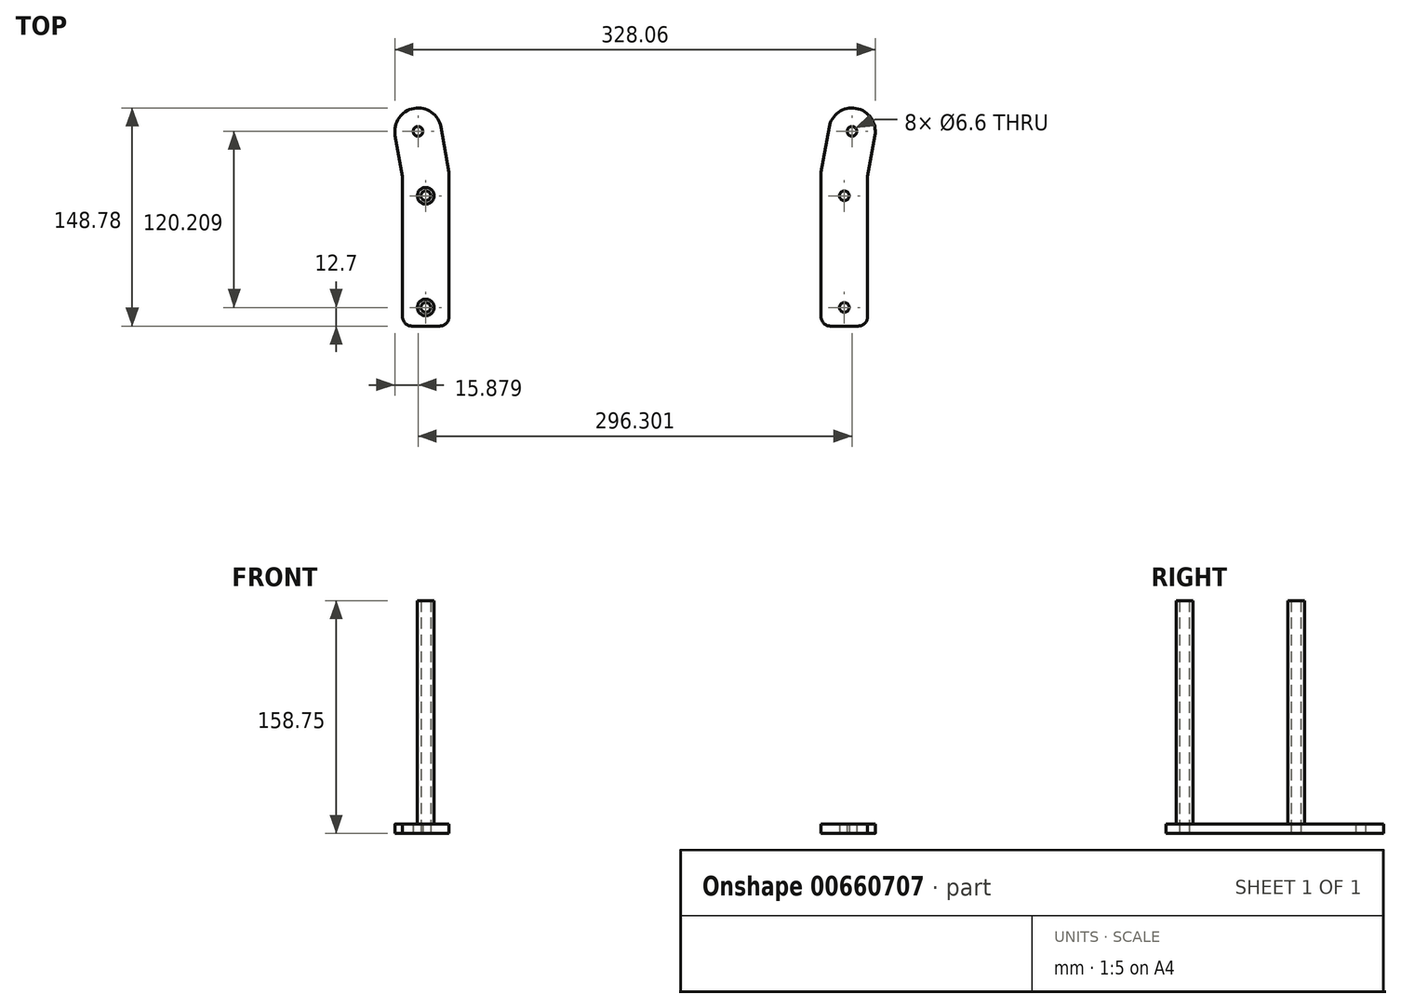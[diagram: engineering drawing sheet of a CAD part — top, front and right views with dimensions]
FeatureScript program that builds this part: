
annotation { "Feature Type Name" : "Feature", "Feature Type Description" : "" }
export const myFeature = defineFeature(function(context is Context, id is Id, definition is map)
    precondition{}
    {
        {
            var Q0;
            Q0=qCreatedBy(makeId("Top.planeOp"),FACE);
            var sketch = newSketch(context, id + "F0", { "sketchPlane" : qUnion([Q0])});
            skLineSegment(sketch, "E0", {"start": v(-163.78, 28.55) * mm, "end": v(-158.85, 0.55) * mm});
            skLineSegment(sketch, "E1", {"start": v(-158.75, -0.56) * mm, "end": v(-158.75, -95.25) * mm});
            skLineSegment(sketch, "E2", {"start": v(-152.4, -101.6) * mm, "end": v(-133.35, -101.6) * mm});
            skLineSegment(sketch, "E3", {"start": v(-127, -95.25) * mm, "end": v(-127, 0) * mm});
            skLineSegment(sketch, "E4", {"start": v(-158.75, 0) * mm, "end": v(-127, 0) * mm, "construction": true});
            skLineSegment(sketch, "E5", {"start": v(-142.88, 0) * mm, "end": v(-142.88, -101.6) * mm, "construction": true});
            skCircle(sketch, "E6", {"center": v(-142.88, -12.7) * mm, "radius": 3.3 * mm});
            skCircle(sketch, "E7", {"center": v(-142.88, -88.9) * mm, "radius": 3.3 * mm});
            skLineSegment(sketch, "E8", {"start": v(-142.88, -12.7) * mm, "end": v(-142.88, -88.9) * mm, "construction": true});
            skPoint(sketch, "E9", {"position": v(-142.88, -50.8) * mm});
            skLineSegment(sketch, "E10", {"start": v(0, 30.92) * mm, "end": v(0, -30.92) * mm, "construction": true});
            skPoint(sketch, "E11", {"position": v(0, 0) * mm});
            skPoint(sketch, "E12.visualSharp", {"position": v(-127, -101.6) * mm});
            skPoint(sketch, "E13.visualSharp", {"position": v(-158.75, -101.6) * mm});
            skArc(sketch, "E14", {"start": v(-132.52, 34.07) * mm, "mid": v(-150.9, 46.94) * mm, "end": v(-163.78, 28.55) * mm});
            skLineSegment(sketch, "E15", {"start": v(-132.52, 34.07) * mm, "end": v(-163.78, 28.55) * mm, "construction": true});
            skLineSegment(sketch, "E16", {"start": v(-132.52, 34.07) * mm, "end": v(-127.1, 3.32) * mm});
            skLineSegment(sketch, "E17", {"start": v(-127, 0) * mm, "end": v(-127, 2.22) * mm});
            skPoint(sketch, "E18.visualSharp", {"position": v(-127, 2.78) * mm});
            skArc(sketch, "E18.filletArc", {"start": v(-127, 2.22) * mm, "mid": v(-127.02, 2.78) * mm, "end": v(-127.1, 3.32) * mm});
            skPoint(sketch, "E19.visualSharp", {"position": v(-158.75, 0) * mm});
            skArc(sketch, "E19.filletArc", {"start": v(-158.75, -0.56) * mm, "mid": v(-158.77, 0) * mm, "end": v(-158.85, 0.55) * mm});
            skLineSegment(sketch, "E20", {"start": v(0, 0) * mm, "end": v(-127, 0) * mm, "construction": true});
            skLineSegment(sketch, "E21", {"start": v(-142.88, 0) * mm, "end": v(-148.15, 31.3) * mm, "construction": true});
            skArc(sketch, "E22.filletArc", {"start": v(-158.75, -95.25) * mm, "mid": v(-156.9, -99.74) * mm, "end": v(-152.4, -101.6) * mm});
            skArc(sketch, "E23.filletArc", {"start": v(-133.35, -101.6) * mm, "mid": v(-128.86, -99.74) * mm, "end": v(-127, -95.25) * mm});
            skLineSegment(sketch, "E24.MirrorCS", {"start": v(132.52, 34.07) * mm, "end": v(127.1, 3.32) * mm});
            skArc(sketch, "E25.MirrorCS", {"start": v(132.52, 34.07) * mm, "mid": v(150.9, 46.94) * mm, "end": v(163.78, 28.55) * mm});
            skLineSegment(sketch, "E26.MirrorCS", {"start": v(163.78, 28.55) * mm, "end": v(158.85, 0.55) * mm});
            skArc(sketch, "E27.MirrorCS", {"start": v(158.75, -0.56) * mm, "mid": v(158.77, 0) * mm, "end": v(158.85, 0.55) * mm});
            skLineSegment(sketch, "E28.MirrorCS", {"start": v(158.75, -0.56) * mm, "end": v(158.75, -95.25) * mm});
            skArc(sketch, "E29.MirrorCS", {"start": v(127, 2.22) * mm, "mid": v(127.02, 2.78) * mm, "end": v(127.1, 3.32) * mm});
            skLineSegment(sketch, "E30.MirrorCS", {"start": v(127, 0) * mm, "end": v(127, 2.22) * mm});
            skArc(sketch, "E31.MirrorCS", {"start": v(158.75, -95.25) * mm, "mid": v(156.9, -99.74) * mm, "end": v(152.4, -101.6) * mm});
            skLineSegment(sketch, "E32.MirrorCS", {"start": v(152.4, -101.6) * mm, "end": v(133.35, -101.6) * mm});
            skArc(sketch, "E33.MirrorCS", {"start": v(133.35, -101.6) * mm, "mid": v(128.86, -99.74) * mm, "end": v(127, -95.25) * mm});
            skLineSegment(sketch, "E34.MirrorCS", {"start": v(127, -95.25) * mm, "end": v(127, 0) * mm});
            skCircle(sketch, "E35", {"center": v(-148.15, 31.3) * mm, "radius": 3.3 * mm});
            skCircle(sketch, "E36.MirrorC", {"center": v(148.15, 31.3) * mm, "radius": 3.3 * mm});
            skCircle(sketch, "E37.MirrorC", {"center": v(142.88, -12.7) * mm, "radius": 3.3 * mm});
            skCircle(sketch, "E38.MirrorC", {"center": v(142.88, -88.9) * mm, "radius": 3.3 * mm});
            skSolve(sketch);
        }
        {
            var Q0;
            Q0=makeQuery(id+"F0.imprint","IMPRINT",FACE,{"disambiguationData":[TD([[makeQuery(id+"F0.imprint","IMPRINT",EDGE,{"derivedFrom":sQuery(id+"F0.wireOp",EDGE,"E0")}),1.0]])]});
            var Q1;
            Q1=makeQuery(id+"F0.imprint","IMPRINT",FACE,{"disambiguationData":[TD([[makeQuery(id+"F0.imprint","IMPRINT",EDGE,{"derivedFrom":sQuery(id+"F0.wireOp",EDGE,"0249e478-3a88-4d2c-a210-11c1fa801e9a0.MirrorCS")}),-1.0]])]});
            var Q2;
            Q2=makeQuery(id+"F0.imprint","IMPRINT",FACE,{"disambiguationData":[TD([[makeQuery(id+"F0.imprint","IMPRINT",EDGE,{"derivedFrom":sQuery(id+"F0.wireOp",EDGE,"417904c8-6a04-4207-bfcf-ffdcabad85960.MirrorCS")}),-1.0]])]});
            var Q3;
            Q3=makeQuery(id+"F0.imprint","IMPRINT",FACE,{"disambiguationData":[TD([[makeQuery(id+"F0.imprint","IMPRINT",EDGE,{"derivedFrom":sQuery(id+"F0.wireOp",EDGE,"E24.MirrorCS")}),1.0]])]});
            extrude(context, id + "F1", {"entities" : qUnion([Q0, Q1, Q2, Q3]), "depth" : 6.35 * mm, "offsetDistance" : 25.4 * mm});
        }
        {
            var Q0;
            Q0=makeQuery(id+"F1.opExtrude","CAP_FACE",FACE,{"disambiguationData":[OSD([sQuery(id+"F0.wireOp",EDGE,"E0"),sQuery(id+"F0.wireOp",EDGE,"E1"),sQuery(id+"F0.wireOp",EDGE,"E2"),sQuery(id+"F0.wireOp",EDGE,"E3"),sQuery(id+"F0.wireOp",EDGE,"uViVmrJY-JCsh-tP8L-dt5C-8XgPy4Xd0ImP"),sQuery(id+"F0.wireOp",EDGE,"lWO3sbvZ-g1mz-J9B7-t8hw-3GOGxWjmcKuG"),sQuery(id+"F0.wireOp",EDGE,"E6"),sQuery(id+"F0.wireOp",EDGE,"E7")])],"isStart":false});
            var sketch = newSketch(context, id + "F2", { "sketchPlane" : qUnion([Q0])});
            skCircle(sketch, "E39.0", {"center": v(-142.88, -12.7) * mm, "radius": 3.3 * mm});
            skCircle(sketch, "E40.0", {"center": v(-142.88, -88.9) * mm, "radius": 3.3 * mm});
            skCircle(sketch, "E41", {"center": v(-142.88, -12.7) * mm, "radius": 5.72 * mm});
            skCircle(sketch, "E42", {"center": v(-142.88, -88.9) * mm, "radius": 5.72 * mm});
            skLineSegment(sketch, "E43.0", {"start": v(0, 30.92) * mm, "end": v(0, -30.92) * mm});
            skCircle(sketch, "E44.MirrorC", {"center": v(142.88, -12.7) * mm, "radius": 5.72 * mm});
            skCircle(sketch, "E45.MirrorC", {"center": v(142.88, -88.9) * mm, "radius": 5.72 * mm});
            skCircle(sketch, "E46.MirrorC", {"center": v(142.88, -12.7) * mm, "radius": 3.3 * mm});
            skCircle(sketch, "E47.MirrorC", {"center": v(142.88, -88.9) * mm, "radius": 3.3 * mm});
            skSolve(sketch);
        }
        {
            var Q0;
            Q0=makeQuery(id+"F2.imprint","IMPRINT",FACE,{"disambiguationData":[TD([[makeQuery(id+"F2.imprint","IMPRINT",EDGE,{"derivedFrom":sQuery(id+"F2.wireOp",EDGE,"E39.0")}),-1.0]])]});
            var Q1;
            Q1=makeQuery(id+"F2.imprint","IMPRINT",FACE,{"disambiguationData":[TD([[makeQuery(id+"F2.imprint","IMPRINT",EDGE,{"derivedFrom":sQuery(id+"F2.wireOp",EDGE,"E40.0")}),-1.0]])]});
            var Q2;
            Q2=makeQuery(id+"F2.imprint","IMPRINT",FACE,{"disambiguationData":[TD([[makeQuery(id+"F2.imprint","IMPRINT",EDGE,{"derivedFrom":sQuery(id+"F2.wireOp",EDGE,"E44.MirrorC")}),-1.0]])]});
            var Q3;
            Q3=makeQuery(id+"F2.imprint","IMPRINT",FACE,{"disambiguationData":[TD([[makeQuery(id+"F2.imprint","IMPRINT",EDGE,{"derivedFrom":sQuery(id+"F2.wireOp",EDGE,"E45.MirrorC")}),-1.0]])]});
            extrude(context, id + "F3", {"entities" : qUnion([Q0, Q1, Q2, Q3]), "depth" : 152.4 * mm, "offsetDistance" : 25.4 * mm});
        }
    });
